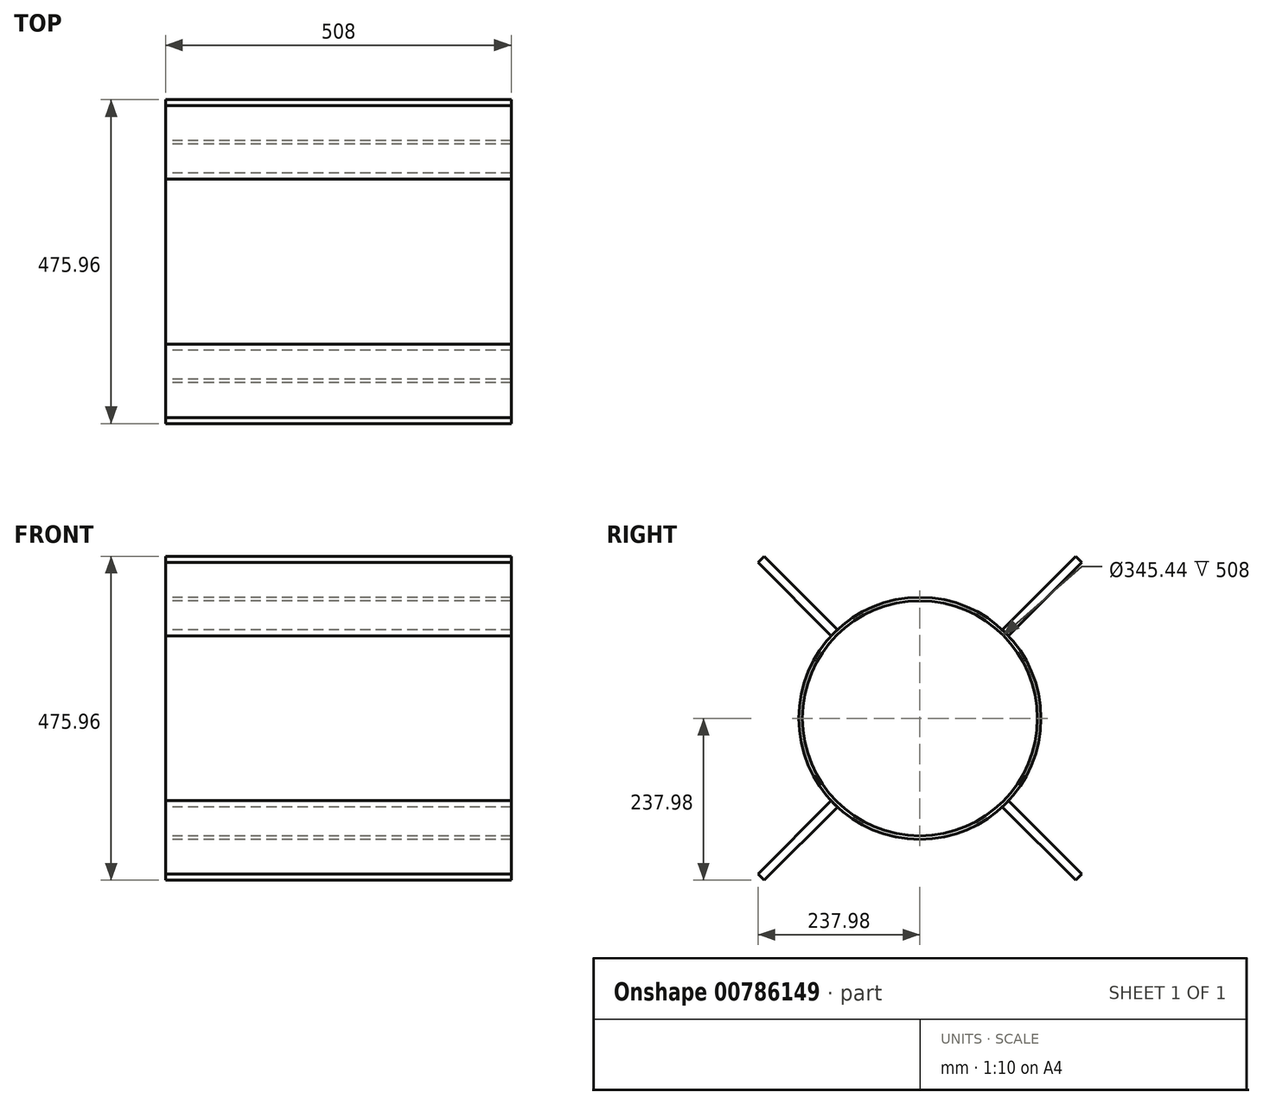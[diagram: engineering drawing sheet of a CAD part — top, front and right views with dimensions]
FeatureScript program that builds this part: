
annotation { "Feature Type Name" : "Feature", "Feature Type Description" : "" }
export const myFeature = defineFeature(function(context is Context, id is Id, definition is map)
    precondition{}
    {
        {
            var Q0;
            Q0=qCreatedBy(makeId("Right.planeOp"),FACE);
            var sketch = newSketch(context, id + "F0", { "sketchPlane" : qUnion([Q0])});
            skCircle(sketch, "E0", {"center": v(0, 0) * mm, "radius": 177.8 * mm});
            skCircle(sketch, "E1", {"center": v(0, 0) * mm, "radius": 172.72 * mm});
            skSolve(sketch);
        }
        {
            var Q0;
            Q0 = qSketchRegion(id + "F0", true);
            extrude(context, id + "F1", {"entities" : qUnion([Q0]), "endBound" : BoundingType.SYMMETRIC, "depth" : 508 * mm, "offsetDistance" : 25.4 * mm});
        }
        {
            var Q0;
            Q0=qCreatedBy(makeId("Right.planeOp"),FACE);
            var sketch = newSketch(context, id + "F2", { "sketchPlane" : qUnion([Q0])});
            skLineSegment(sketch, "E2", {"start": v(-330.2, 6.35) * mm, "end": v(-330.2, -6.35) * mm});
            skCircle(sketch, "E3", {"center": v(0, 0) * mm, "radius": 177.8 * mm});
            skLineSegment(sketch, "E4", {"start": v(-330.2, 6.35) * mm, "end": v(-177.69, 6.35) * mm});
            skLineSegment(sketch, "E5", {"start": v(-330.2, -6.35) * mm, "end": v(-177.69, -6.35) * mm});
            skSolve(sketch);
        }
        {
            var Q0;
            Q0=makeQuery(id+"F2.imprint","IMPRINT",FACE,{"disambiguationData":[TD([[makeQuery(id+"F2.imprint","IMPRINT",EDGE,{"derivedFrom":sQuery(id+"F2.wireOp",EDGE,"E2")}),1.0]])]});
            extrude(context, id + "F3", {"entities" : qUnion([Q0]), "endBound" : BoundingType.SYMMETRIC, "depth" : 508 * mm, "offsetDistance" : 25.4 * mm});
        }
        {
            var Q0;
            Q0=makeQuery(id+"F3.opExtrude","SWEPT_BODY",BODY,{"disambiguationData":[OSD([sQuery(id+"F2.wireOp",EDGE,"E2"),sQuery(id+"F2.wireOp",EDGE,"E3"),sQuery(id+"F2.wireOp",EDGE,"E4"),sQuery(id+"F2.wireOp",EDGE,"E5")])]});
            var Q1;
            Q1=makeQuery(id+"F1.opExtrude","CAP_EDGE",EDGE,{"disambiguationData":[OSD([sQuery(id+"F0.wireOp",EDGE,"E1")])],"isStart":true});
            transform(context, id + "F4", {"entities" : qUnion([Q0]), "transformType" : TransformType.ROTATION, "transformAxis" : qUnion([Q1]), "angle" : 90 * degree, "makeCopy" : false});
        }
        {
            var Q0;
            Q0=makeQuery(id+"F3.opExtrude","SWEPT_BODY",BODY,{"disambiguationData":[OSD([sQuery(id+"F2.wireOp",EDGE,"E2"),sQuery(id+"F2.wireOp",EDGE,"E3"),sQuery(id+"F2.wireOp",EDGE,"E4"),sQuery(id+"F2.wireOp",EDGE,"E5")])]});
            var Q1;
            Q1=makeQuery(id+"F1.opExtrude","CAP_EDGE",EDGE,{"disambiguationData":[OSD([sQuery(id+"F0.wireOp",EDGE,"E0")])],"isStart":true});
            transform(context, id + "F5", {"entities" : qUnion([Q0]), "transformType" : TransformType.ROTATION, "transformAxis" : qUnion([Q1]), "angle" : 180 * degree, "makeCopy" : true});
        }
        {
            var Q0;
            Q0=makeQuery(id+"F3.opExtrude","SWEPT_BODY",BODY,{"disambiguationData":[OSD([sQuery(id+"F2.wireOp",EDGE,"E2"),sQuery(id+"F2.wireOp",EDGE,"E3"),sQuery(id+"F2.wireOp",EDGE,"E4"),sQuery(id+"F2.wireOp",EDGE,"E5")])]});
            var Q1;
            Q1=makeQuery(id+"F5.opPattern","COPY",BODY,{"derivedFrom":makeQuery(id+"F3.opExtrude","SWEPT_BODY",BODY,{"disambiguationData":[OSD([sQuery(id+"F2.wireOp",EDGE,"E2"),sQuery(id+"F2.wireOp",EDGE,"E3"),sQuery(id+"F2.wireOp",EDGE,"E4"),sQuery(id+"F2.wireOp",EDGE,"E5")])]}),"instanceName":"1"});
            var Q2;
            Q2=makeQuery(id+"F1.opExtrude","CAP_EDGE",EDGE,{"disambiguationData":[OSD([sQuery(id+"F0.wireOp",EDGE,"E0")])],"isStart":true});
            transform(context, id + "F6", {"entities" : qUnion([Q0, Q1]), "transformType" : TransformType.ROTATION, "transformAxis" : qUnion([Q2]), "angle" : 45 * degree, "makeCopy" : false});
        }
        {
            var Q0;
            Q0=makeQuery(id+"F3.opExtrude","SWEPT_BODY",BODY,{"disambiguationData":[OSD([sQuery(id+"F2.wireOp",EDGE,"E2"),sQuery(id+"F2.wireOp",EDGE,"E3"),sQuery(id+"F2.wireOp",EDGE,"E4"),sQuery(id+"F2.wireOp",EDGE,"E5")])]});
            var Q1;
            Q1=makeQuery(id+"F5.opPattern","COPY",BODY,{"derivedFrom":makeQuery(id+"F3.opExtrude","SWEPT_BODY",BODY,{"disambiguationData":[OSD([sQuery(id+"F2.wireOp",EDGE,"E2"),sQuery(id+"F2.wireOp",EDGE,"E3"),sQuery(id+"F2.wireOp",EDGE,"E4"),sQuery(id+"F2.wireOp",EDGE,"E5")])]}),"instanceName":"1"});
            var Q2;
            Q2=makeQuery(id+"F1.opExtrude","CAP_EDGE",EDGE,{"disambiguationData":[OSD([sQuery(id+"F0.wireOp",EDGE,"E0")])],"isStart":true});
            transform(context, id + "F7", {"entities" : qUnion([Q0, Q1]), "transformType" : TransformType.ROTATION, "transformAxis" : qUnion([Q2]), "angle" : 90 * degree, "makeCopy" : true});
        }
    });
